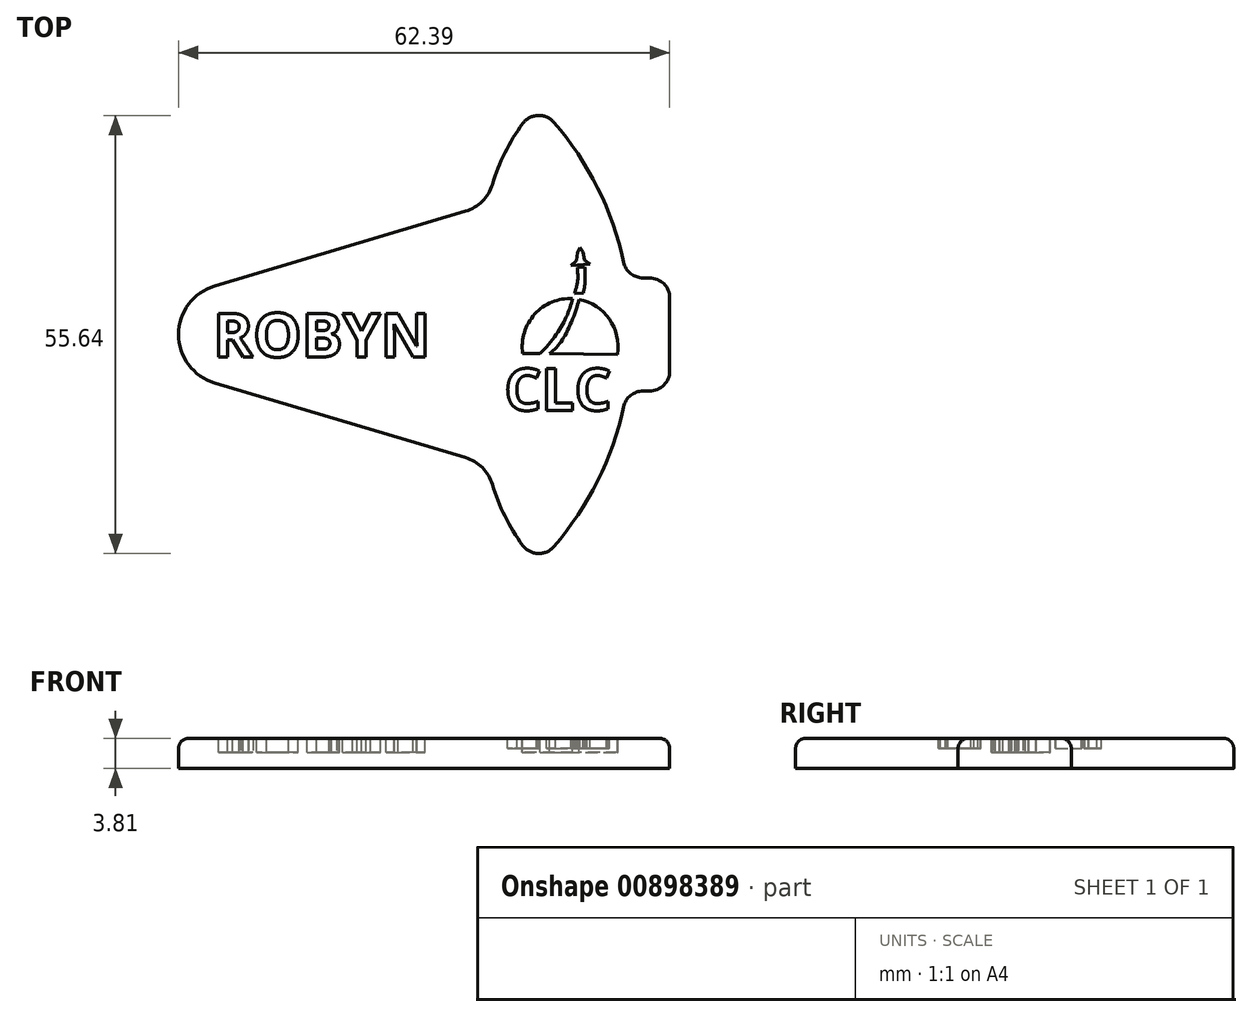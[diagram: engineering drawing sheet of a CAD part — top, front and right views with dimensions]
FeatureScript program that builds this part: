
annotation { "Feature Type Name" : "Feature", "Feature Type Description" : "" }
export const myFeature = defineFeature(function(context is Context, id is Id, definition is map)
    precondition{}
    {
        {
            var Q0;
            Q0=qCreatedBy(makeId("Top.planeOp"),FACE);
            var sketch = newSketch(context, id + "F0", { "sketchPlane" : qUnion([Q0])});
            skLineSegment(sketch, "E0", {"start": v(11.89, 15.65) * mm, "end": v(-19.97, 6.16) * mm});
            skArc(sketch, "E1", {"start": v(19.16, 26.79) * mm, "mid": v(16.9, 23.09) * mm, "end": v(15.3, 19.06) * mm});
            skArc(sketch, "E2", {"start": v(31.97, 9.2) * mm, "mid": v(28.67, 18.62) * mm, "end": v(23.13, 26.94) * mm});
            skArc(sketch, "E3.filletArc", {"start": v(23.13, 26.94) * mm, "mid": v(21.1, 27.82) * mm, "end": v(19.16, 26.79) * mm});
            skPoint(sketch, "E4.visualSharp", {"position": v(14.67, 16.48) * mm});
            skArc(sketch, "E4.filletArc", {"start": v(11.89, 15.65) * mm, "mid": v(14.03, 16.92) * mm, "end": v(15.3, 19.06) * mm});
            skLineSegment(sketch, "E5", {"start": v(0, 0) * mm, "end": v(38.6, 0) * mm, "construction": true});
            skLineSegment(sketch, "E6.bottom", {"start": v(35.29, 7.18) * mm, "end": v(34.45, 7.18) * mm});
            skLineSegment(sketch, "E6.left", {"start": v(37.83, 4.64) * mm, "end": v(37.83, 0) * mm});
            skPoint(sketch, "E6.middle", {"position": v(32.86, 0) * mm});
            skPoint(sketch, "E7.newPointB", {"position": v(27.89, 7.18) * mm});
            skArc(sketch, "E7.filletArc", {"start": v(31.97, 9.2) * mm, "mid": v(32.86, 7.75) * mm, "end": v(34.45, 7.18) * mm});
            skPoint(sketch, "E8.visualSharp", {"position": v(37.83, 7.18) * mm});
            skArc(sketch, "E8.filletArc", {"start": v(37.83, 4.64) * mm, "mid": v(37.09, 6.44) * mm, "end": v(35.29, 7.18) * mm});
            skPoint(sketch, "E9.orphan", {"position": v(37.83, -7.18) * mm});
            skLineSegment(sketch, "E10.MirrorCS", {"start": v(11.89, -15.65) * mm, "end": v(-19.97, -6.16) * mm});
            skArc(sketch, "E11.MirrorCS", {"start": v(11.89, -15.65) * mm, "mid": v(14.03, -16.92) * mm, "end": v(15.3, -19.06) * mm});
            skArc(sketch, "E12.MirrorCS", {"start": v(19.16, -26.79) * mm, "mid": v(16.9, -23.09) * mm, "end": v(15.3, -19.06) * mm});
            skArc(sketch, "E13.MirrorCS", {"start": v(23.13, -26.94) * mm, "mid": v(21.1, -27.82) * mm, "end": v(19.16, -26.79) * mm});
            skArc(sketch, "E14.MirrorCS", {"start": v(31.97, -9.2) * mm, "mid": v(28.67, -18.62) * mm, "end": v(23.13, -26.94) * mm});
            skArc(sketch, "E15.MirrorCS", {"start": v(31.97, -9.2) * mm, "mid": v(32.86, -7.75) * mm, "end": v(34.45, -7.18) * mm});
            skLineSegment(sketch, "E16.MirrorCS", {"start": v(35.29, -7.18) * mm, "end": v(34.45, -7.18) * mm});
            skArc(sketch, "E17.MirrorCS", {"start": v(37.83, -4.64) * mm, "mid": v(37.09, -6.44) * mm, "end": v(35.29, -7.18) * mm});
            skLineSegment(sketch, "E18.MirrorCS", {"start": v(37.83, -4.64) * mm, "end": v(37.83, 0) * mm});
            skPoint(sketch, "E19.newPointA", {"position": v(-20.8, 5.9) * mm});
            skPoint(sketch, "E19.newPointB", {"position": v(-20.8, -5.9) * mm});
            skArc(sketch, "E19.filletArc", {"start": v(-19.97, 6.16) * mm, "mid": v(-24.56, 0) * mm, "end": v(-19.97, -6.16) * mm});
            skSolve(sketch);
        }
        {
            var Q0;
            Q0=qSketchRegion(id+"F0",true);
            extrude(context, id + "F1", {"entities" : qUnion([Q0]), "depth" : 3.8 * mm, "offsetDistance" : 25.4 * mm});
        }
        {
            var Q0;
            Q0=makeQuery(id+"F1.opExtrude","CAP_FACE",FACE,{"disambiguationData":[OSD([sQuery(id+"F0.wireOp",EDGE,"E0"),sQuery(id+"F0.wireOp",EDGE,"E1"),sQuery(id+"F0.wireOp",EDGE,"E2"),sQuery(id+"F0.wireOp",EDGE,"E3.filletArc"),sQuery(id+"F0.wireOp",EDGE,"E4.filletArc"),sQuery(id+"F0.wireOp",EDGE,"E6.bottom"),sQuery(id+"F0.wireOp",EDGE,"E6.left"),sQuery(id+"F0.wireOp",EDGE,"E7.filletArc"),sQuery(id+"F0.wireOp",EDGE,"E8.filletArc"),sQuery(id+"F0.wireOp",EDGE,"E10.MirrorCS"),sQuery(id+"F0.wireOp",EDGE,"E11.MirrorCS"),sQuery(id+"F0.wireOp",EDGE,"E12.MirrorCS"),sQuery(id+"F0.wireOp",EDGE,"E13.MirrorCS"),sQuery(id+"F0.wireOp",EDGE,"E14.MirrorCS"),sQuery(id+"F0.wireOp",EDGE,"E15.MirrorCS"),sQuery(id+"F0.wireOp",EDGE,"E16.MirrorCS"),sQuery(id+"F0.wireOp",EDGE,"E17.MirrorCS"),sQuery(id+"F0.wireOp",EDGE,"E18.MirrorCS"),sQuery(id+"F0.wireOp",EDGE,"E19.filletArc")])],"isStart":false});
            var sketch = newSketch(context, id + "F2", { "sketchPlane" : qUnion([Q0])});
            skText(sketch, "E20", { "text": "ROBYN", "fontName": "OpenSans-Bold.ttf"});
            skArc(sketch, "E21", {"start": v(31.17, -2.53) * mm, "mid": v(30.17, 1.95) * mm, "end": v(26.32, 4.45) * mm});
            skLineSegment(sketch, "E22", {"start": v(19.16, -2.42) * mm, "end": v(21.34, -2.44) * mm});
            skFitSpline(sketch, "E23", {"points": [v(21.34, -2.44) * mm, v(24.33, 1.49) * mm, v(25.51, 4.55) * mm], "startDerivative": vector(6.62, 6.16) * mm, "endDerivative": vector(1.74, 6.77) * mm});
            skFitSpline(sketch, "E24", {"points": [v(22.55, -2.45) * mm, v(24.6, 0) * mm, v(26.32, 4.45) * mm], "startDerivative": vector(5.89, 4.59) * mm, "endDerivative": vector(1.7, 6.96) * mm});
            skLineSegment(sketch, "E25.trimOffspring", {"start": v(22.55, -2.45) * mm, "end": v(31.17, -2.53) * mm});
            skArc(sketch, "E26.trimOffspring", {"start": v(25.51, 4.55) * mm, "mid": v(20.68, 2.57) * mm, "end": v(19.16, -2.42) * mm});
            const initialGuessF2  = {"E20": [-0.0202, -0.00285, 1, 0, 0.00558]};
            skSetInitialGuess(sketch, initialGuessF2);
            skSolve(sketch);
        }
        {
            var Q0;
            Q0=qSketchRegion(id+"F2",true);
            extrude(context, id + "F3", {"entities" : qUnion([Q0]), "operationType" : NewBodyOperationType.REMOVE, "oppositeDirection" : true, "depth" : 1.78 * mm, "offsetDistance" : 25.4 * mm});
        }
        {
            var Q0;
            Q0=makeQuery(id+"F1.opExtrude","CAP_EDGE",EDGE,{"disambiguationData":[OSD([sQuery(id+"F0.wireOp",EDGE,"E0")])],"isStart":false});
            fillet(context, id + "F4", {"entities" : qUnion([Q0]), "radius" : 1.27 * mm, "tangentPropagation" : true, "allowEdgeOverflow" : false});
        }
        {
            var Q0;
            {var subQ0=sQuery(id+"F0.wireOp",EDGE,"E19.filletArc");var subQ1=sQuery(id+"F0.wireOp",EDGE,"E16.MirrorCS");var subQ2=sQuery(id+"F0.wireOp",EDGE,"E15.MirrorCS");var subQ3=sQuery(id+"F0.wireOp",EDGE,"E14.MirrorCS");var subQ4=sQuery(id+"F0.wireOp",EDGE,"E13.MirrorCS");var subQ5=sQuery(id+"F0.wireOp",EDGE,"E12.MirrorCS");var subQ6=sQuery(id+"F0.wireOp",EDGE,"E11.MirrorCS");var subQ7=sQuery(id+"F0.wireOp",EDGE,"E17.MirrorCS");var subQ8=sQuery(id+"F0.wireOp",EDGE,"E2");var subQ9=sQuery(id+"F0.wireOp",EDGE,"E1");var subQ10=sQuery(id+"F0.wireOp",EDGE,"E3.filletArc");var subQ11=sQuery(id+"F0.wireOp",EDGE,"E0");var subQ12=sQuery(id+"F0.wireOp",EDGE,"E10.MirrorCS");var subQ13=sQuery(id+"F0.wireOp",EDGE,"E4.filletArc");var subQ14=sQuery(id+"F0.wireOp",EDGE,"E6.bottom");var subQ15=sQuery(id+"F0.wireOp",EDGE,"E18.MirrorCS");var subQ16=sQuery(id+"F0.wireOp",EDGE,"E6.left");var subQ17=sQuery(id+"F0.wireOp",EDGE,"E7.filletArc");var subQ18=sQuery(id+"F0.wireOp",EDGE,"E8.filletArc");Q0=makeQuery(id+"F3.boolean.opBoolean","SPLIT",FACE,{"disambiguationData":[TD([makeQuery(id+"F1.opExtrude","SWEPT_FACE",FACE,{"disambiguationData":[OSD([subQ11])]})])],"derivedFrom":makeQuery(id+"F1.opExtrude","CAP_FACE",FACE,{"disambiguationData":[OSD([subQ11,subQ9,subQ8,subQ10,subQ13,subQ14,subQ16,subQ17,subQ18,subQ12,subQ6,subQ5,subQ4,subQ3,subQ2,subQ1,subQ7,subQ15,subQ0])],"isStart":false})});}
            var sketch = newSketch(context, id + "F5", { "sketchPlane" : qUnion([Q0])});
            skFitSpline(sketch, "E27", {"points": [v(25.74, 5.18) * mm, v(26.14, 6.78) * mm, v(26.1, 8.49) * mm], "startDerivative": vector(0.75, 2.74) * mm, "endDerivative": vector(-0.13, 3.1) * mm});
            skFitSpline(sketch, "E28", {"points": [v(26.85, 5.24) * mm, v(27.1, 6.9) * mm, v(27.03, 8.54) * mm], "startDerivative": vector(0.63, 2.73) * mm, "endDerivative": vector(-0.23, 3.22) * mm});
            skLineSegment(sketch, "E29", {"start": v(26.1, 8.49) * mm, "end": v(27.03, 8.54) * mm});
            skLineSegment(sketch, "E30", {"start": v(25.74, 5.18) * mm, "end": v(26.85, 5.24) * mm});
            skLineSegment(sketch, "E31", {"start": v(25.32, 8.79) * mm, "end": v(27.68, 8.93) * mm});
            skLineSegment(sketch, "E32", {"start": v(27.68, 8.93) * mm, "end": v(26.98, 9.44) * mm});
            skLineSegment(sketch, "E33", {"start": v(26.98, 9.44) * mm, "end": v(26.82, 10.48) * mm});
            skLineSegment(sketch, "E34", {"start": v(26.82, 10.48) * mm, "end": v(26.45, 11.04) * mm});
            skLineSegment(sketch, "E35", {"start": v(26.45, 11.04) * mm, "end": v(26.1, 10.43) * mm});
            skLineSegment(sketch, "E36", {"start": v(26.1, 10.43) * mm, "end": v(26.01, 9.39) * mm});
            skLineSegment(sketch, "E37", {"start": v(26.01, 9.39) * mm, "end": v(25.32, 8.79) * mm});
            skSolve(sketch);
        }
        {
            var Q0;
            Q0=makeQuery(id+"F5.imprint","IMPRINT",FACE,{"disambiguationData":[TD([[makeQuery(id+"F5.imprint","IMPRINT",EDGE,{"derivedFrom":sQuery(id+"F5.wireOp",EDGE,"E27")}),-1.0]])]});
            var Q1;
            Q1=makeQuery(id+"F5.imprint","IMPRINT",FACE,{"disambiguationData":[TD([[makeQuery(id+"F5.imprint","IMPRINT",EDGE,{"derivedFrom":sQuery(id+"F5.wireOp",EDGE,"E31")}),1.0]])]});
            extrude(context, id + "F6", {"entities" : qUnion([Q0, Q1]), "operationType" : NewBodyOperationType.REMOVE, "oppositeDirection" : true, "depth" : 1.27 * mm, "offsetDistance" : 25.4 * mm});
        }
        {
            var Q0;
            Q0=makeQuery(id+"F5.imprint","IMPRINT",FACE,{"disambiguationData":[TD([[makeQuery(id+"F5.imprint","IMPRINT",EDGE,{"derivedFrom":sQuery(id+"F5.wireOp",EDGE,"E27")}),1.0]])]});
            var sketch = newSketch(context, id + "F7", { "sketchPlane" : qUnion([Q0])});
            skText(sketch, "E38", { "text": "CLC", "fontName": "OpenSans-Bold.ttf"});
            const initialGuessF7  = {"E38": [0.01683, -0.00964, 1, 0, 0.00533]};
            skSetInitialGuess(sketch, initialGuessF7);
            skSolve(sketch);
        }
        {
            var Q0;
            Q0=qSketchRegion(id+"F7",true);
            extrude(context, id + "F8", {"entities" : qUnion([Q0]), "operationType" : NewBodyOperationType.REMOVE, "oppositeDirection" : true, "depth" : 1.27 * mm, "offsetDistance" : 25.4 * mm});
        }
    });
